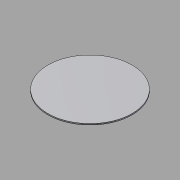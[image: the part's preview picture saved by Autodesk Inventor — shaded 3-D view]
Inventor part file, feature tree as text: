
AUTODESK INVENTOR PART (.ipt)
format: ipt  version: 2015 (Build 190159000, 159)  size: 83,968 bytes
history: native  units: mm
features: extrude x1, sketch x1
ambient origin geometry x8: Origin, YZ Plane, XZ Plane, XY Plane, X Axis, Y Axis, Z Axis, Center Point
bodies: Solid1 (feature_tree)
feature tree (2):
  extrude  "Extrusion1"  Depth=1.0mm TaperAngle=0.0deg
  sketch  "Sketch1"  dims[d0=68.0mm d1=1.0mm d2=0.0mm]
